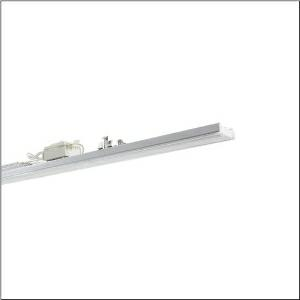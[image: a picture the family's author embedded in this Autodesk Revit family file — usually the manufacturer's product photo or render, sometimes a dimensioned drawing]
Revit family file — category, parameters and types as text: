
# Revit family: licross_r__21_recessed_ho_52te18dn4e5m_8491
name_source: partatom
category: Lighting Fixtures
units: mm (PartAtom-declared; Revit-internal decimal feet)

## family parameters
Cut with Voids When Loaded = No
Host = Face
Light Source = No
Part Type = Normal
Room Calculation Point = No
Round Connector Dimension = Use Diameter
Shared = No

## types (1)
- --- (1 x LED, 14850 lm, 84.6 W, 4000K)
    Apparent Load = 85 VA
    CIE Flux Codes = 75 94 99 100 100
    Color Rendering = 80
    Color Temperature = 4000K
    Default Elevation = 1800 mm
    Description = Licross® 21 Recessed HO, luminaire insert, of sheet steel, galvanised, coil coated, white, length: 1.500mm, width: 66mm, height: 67mm, LED rated luminous flux: 14.850lm, light colour: 840, control gear: DALI 2, with plug, 5-pole, with phase selection, mains connection: 220..240V, AC, 50/60Hz, rated input power: 85W, halogen-free wiring, primary light control with lens, of plastic, primary optical cover: cover, of PMMA, light emission: direct distribution, primary light characteristic: symmetric, protection rating (complete): IP54, insulation class (complete): insulation class I (protective earthing), certification: CE, ENEC, VDE, UKCA, protection symbol: D if used in an environment with non-conductive dust loads with corresponding accessories, impact resistance: IK06, permissible ambient temperature for indoor applications: -25..+30°C, corresponds to IFS (International Featured Standards) requirements for safety and quality in the food industry, reducing of maximum allowable ambient temperature of 5°C with ceiling mounting, LABS conformity tested according to VDMA 24364:2018-05, packaging unit: 1 piece
    Height = 58 mm
    Lamp = 1 x LED
    Lamp Light Flux = 14850 lm
    Lamp Power = 84.6 W
    Lamp count = 1
    Length = 1500 mm
    Luminous efficacy = 176 lm/W
    Manufacturer = Siteco
    ModVariant = No
    Model = 52TE18DN4E5M
    Mounting Place = Ceiling
    Mounting Type = Pendant
    Number of Poles = 1
    OnlyDefault = Yes
    Power Factor = 1
    Product Name = Licross® 21 Recessed HO
    Product group = luminaire insert
    ProductGroupID = 902
    Protection Class = Protection class I
    Protection Degree = IP 54
    RLX_Detail_Level = 1
    RLX_Emergency_Light_Flux = 0 lm
    RLX_Emergency_Type = 0
    RLX_Emergency_Type_DB = No
    RlxData = <blob elided: 24741 chars, md5=85ffb98c>
    Socket = socket
    Standby Power = 0 W
    System Light Flux = 14850 lm
    System Power = 85 W
    Type Comments = factory setting: luminous flux: 100 % | dim-lin: 254 | 484 mA
    Type Image = l_1296930.jpg
    URL = http://relux.com
    VarID = @adj_125710
    Voltage = 0 V
    Weight = 0.00 kg
    Width = 66 mm

## geometry (parser evidence)
native form markers: Blend x4, Sweep x11
no freeform markers — native parametric forms only
